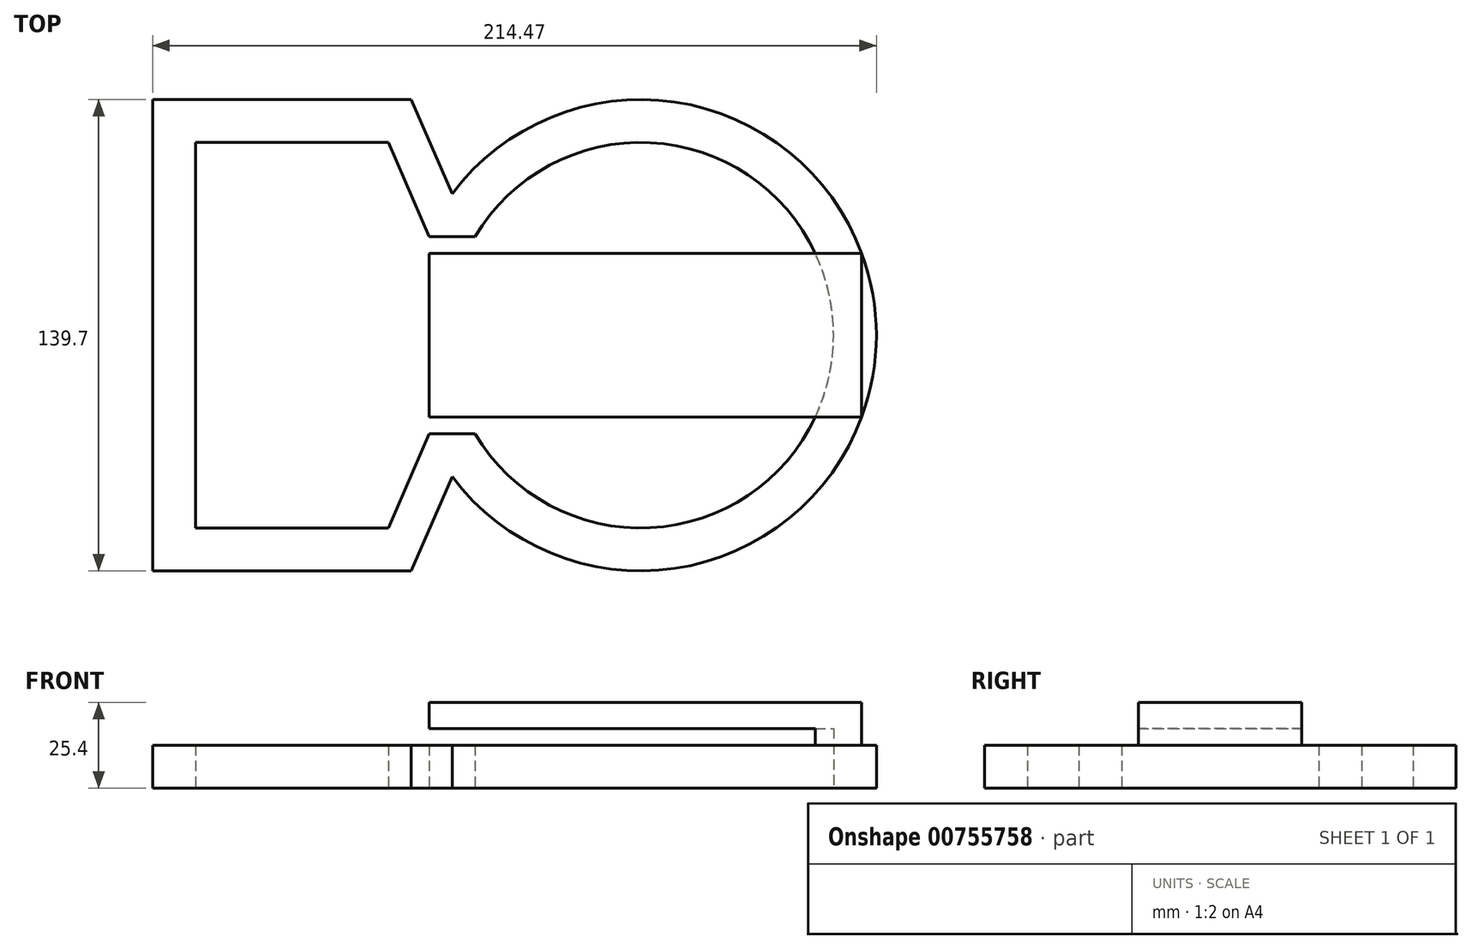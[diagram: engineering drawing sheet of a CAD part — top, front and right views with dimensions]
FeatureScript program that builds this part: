
annotation { "Feature Type Name" : "Feature", "Feature Type Description" : "" }
export const myFeature = defineFeature(function(context is Context, id is Id, definition is map)
    precondition{}
    {
        {
            assignVariable(context, id + "F0", {"name" : "Thickness", "anyValue" : 12.7 * mm});
        }
        {
            assignVariable(context, id + "F1", {"name" : "smallGap", "anyValue" : 5 * mm});
        }
        {
            var Q0;
            Q0=qCreatedBy(makeId("Top.planeOp"),FACE);
            var sketch = newSketch(context, id + "F2", { "sketchPlane" : qUnion([Q0])});
            skLineSegment(sketch, "E0", {"start": v(-80.03, 59.07) * mm, "end": v(-80.03, -55.23) * mm});
            skLineSegment(sketch, "E1", {"start": v(-80.03, 59.07) * mm, "end": v(-22.88, 59.07) * mm});
            skLineSegment(sketch, "E2", {"start": v(-80.03, -55.23) * mm, "end": v(-22.88, -55.23) * mm});
            skPoint(sketch, "E3", {"position": v(-80.03, 1.92) * mm});
            skLineSegment(sketch, "E4", {"start": v(-22.88, 59.07) * mm, "end": v(-10.74, 31.13) * mm});
            skPoint(sketch, "E5", {"position": v(-3.83, -55.23) * mm});
            skPoint(sketch, "E6", {"position": v(-3.83, 1.92) * mm});
            skArc(sketch, "E7", {"start": v(2.77, -27.3) * mm, "mid": v(109.04, 1.92) * mm, "end": v(2.77, 31.13) * mm});
            skLineSegment(sketch, "E8", {"start": v(-92.73, 71.77) * mm, "end": v(-92.73, -67.93) * mm});
            skLineSegment(sketch, "E9", {"start": v(-16.13, -67.93) * mm, "end": v(-92.73, -67.93) * mm});
            skLineSegment(sketch, "E10", {"start": v(-92.73, 71.77) * mm, "end": v(-16.13, 71.77) * mm});
            skLineSegment(sketch, "E11", {"start": v(-16.13, 71.77) * mm, "end": v(-3.99, 43.83) * mm});
            skArc(sketch, "E12", {"start": v(-3.99, 43.83) * mm, "mid": v(121.74, 1.92) * mm, "end": v(-3.99, -40) * mm});
            skLineSegment(sketch, "E13", {"start": v(-22.88, 59.07) * mm, "end": v(-16.13, 71.77) * mm});
            skLineSegment(sketch, "E14", {"start": v(2.77, 31.13) * mm, "end": v(-10.74, 31.13) * mm});
            skPoint(sketch, "E15", {"position": v(-3.99, 31.13) * mm});
            skLineSegment(sketch, "E16", {"start": v(-10.74, -27.3) * mm, "end": v(-22.88, -55.23) * mm});
            skLineSegment(sketch, "E17", {"start": v(2.77, -27.3) * mm, "end": v(-10.74, -27.3) * mm});
            skLineSegment(sketch, "E18", {"start": v(-16.13, -67.93) * mm, "end": v(-3.99, -40) * mm});
            skSolve(sketch);
        }
        {
            var Q0;
            Q0=makeQuery(id+"F2.imprint","IMPRINT",FACE,{"disambiguationData":[TD([[makeQuery(id+"F2.imprint","IMPRINT",EDGE,{"derivedFrom":sQuery(id+"F2.wireOp",EDGE,"E0")}),-1.0]])]});
            extrude(context, id + "F3", {"entities" : qUnion([Q0]), "depth" : getVariable(context, 'Thickness'), "offsetDistance" : 25 * mm});
        }
        {
            var Q0;
            Q0=makeQuery(id+"F3.opExtrude","CAP_FACE",FACE,{"disambiguationData":[OSD([sQuery(id+"F2.wireOp",EDGE,"E0"),sQuery(id+"F2.wireOp",EDGE,"E1"),sQuery(id+"F2.wireOp",EDGE,"E2"),sQuery(id+"F2.wireOp",EDGE,"E4"),sQuery(id+"F2.wireOp",EDGE,"E7"),sQuery(id+"F2.wireOp",EDGE,"E8"),sQuery(id+"F2.wireOp",EDGE,"E9"),sQuery(id+"F2.wireOp",EDGE,"E10"),sQuery(id+"F2.wireOp",EDGE,"E11"),sQuery(id+"F2.wireOp",EDGE,"E12"),sQuery(id+"F2.wireOp",EDGE,"E14"),sQuery(id+"F2.wireOp",EDGE,"E16"),sQuery(id+"F2.wireOp",EDGE,"E17"),sQuery(id+"F2.wireOp",EDGE,"E18")])],"isStart":false});
            var sketch = newSketch(context, id + "F4", { "sketchPlane" : qUnion([Q0])});
            skLineSegment(sketch, "E19.bottom", {"start": v(-10.74, 26.13) * mm, "end": v(117.4, 26.13) * mm});
            skLineSegment(sketch, "E19.top", {"start": v(-10.74, -22.3) * mm, "end": v(117.4, -22.3) * mm});
            skLineSegment(sketch, "E19.left", {"start": v(-10.74, 26.13) * mm, "end": v(-10.74, -22.3) * mm});
            skLineSegment(sketch, "E19.right", {"start": v(117.4, 26.13) * mm, "end": v(117.4, -22.3) * mm});
            skSolve(sketch);
        }
        {
            var Q0;
            Q0=makeQuery(id+"F4.imprint","IMPRINT",FACE,{"disambiguationData":[TD([[makeQuery(id+"F4.imprint","IMPRINT",EDGE,{"derivedFrom":sQuery(id+"F4.wireOp",EDGE,"9zWp7met-CPeg-nwWE-BQaW-SqbrkutXE2nB.right")}),1.0]])]});
            var Q1;
            {var subQ1=sQuery(id+"F4.wireOp",EDGE,"9zWp7met-CPeg-nwWE-BQaW-SqbrkutXE2nB.right");Q1=makeQuery(id+"F4.imprint","IMPRINT",FACE,{"disambiguationData":[TD([[makeQuery(id+"F4.imprint","IMPRINT",EDGE,{"derivedFrom":subQ1}),-1.0]])]});}
            var Q2;
            {var subQ0=sQuery(id+"F4.wireOp",EDGE,"E19.left");Q2=makeQuery(id+"F4.imprint","IMPRINT",FACE,{"disambiguationData":[TD([[makeQuery(id+"F4.imprint","IMPRINT",EDGE,{"derivedFrom":subQ0}),1.0]])]});}
            var Q3;
            {var subQ0=sQuery(id+"F4.wireOp",EDGE,"E19.right");Q3=makeQuery(id+"F4.imprint","IMPRINT",FACE,{"disambiguationData":[TD([[makeQuery(id+"F4.imprint","IMPRINT",EDGE,{"derivedFrom":subQ0}),-1.0]])]});}
            extrude(context, id + "F5", {"entities" : qUnion([Q0, Q1, Q2, Q3]), "operationType" : NewBodyOperationType.ADD, "depth" : getVariable(context, 'Thickness'), "offsetDistance" : 25 * mm});
        }
        {
            var Q0;
            Q0=makeQuery(id+"F5.opExtrude","CAP_FACE",FACE,{"disambiguationData":[OSD([sQuery(id+"F4.wireOp",EDGE,"E19.bottom"),sQuery(id+"F4.wireOp",EDGE,"E19.top"),sQuery(id+"F4.wireOp",EDGE,"E19.left"),sQuery(id+"F4.wireOp",EDGE,"E19.right")])],"isStart":true});
            extrude(context, id + "F6", {"entities" : qUnion([Q0]), "operationType" : NewBodyOperationType.REMOVE, "oppositeDirection" : true, "depth" : getVariable(context, 'smallGap'), "offsetDistance" : 25 * mm});
        }
    });
